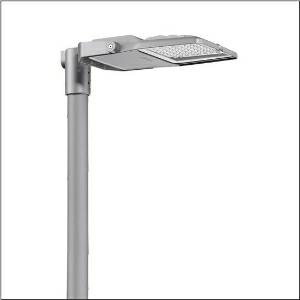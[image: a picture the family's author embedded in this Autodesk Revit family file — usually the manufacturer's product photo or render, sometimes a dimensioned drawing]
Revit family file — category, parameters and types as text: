
# Revit family: floodlight_fl_21_mini___pl43_5xa7775c2a3a_cdc0
name_source: partatom
category: Lighting Fixtures
units: mm (PartAtom-declared; Revit-internal decimal feet)

## family parameters
Cut with Voids When Loaded = No
Host = Face
Light Source = No
Part Type = Normal
Room Calculation Point = No
Round Connector Dimension = Use Diameter
Shared = No

## types (1)
- --- (1 x LED, 12500 lm, 89 W, 3000K)
    Apparent Load = 89 VA
    CIE Flux Codes = 27 78 99 100 100
    Color Rendering = 70
    Color Temperature = 3000K
    Default Elevation = 1800 mm
    Description = Floodlight FL 21 mini, floodlight, primary light control with lens, of PMMA, primary optical cover: protective disc, of toughened safety glass, transparent, light distribution: PL43, light emission: direct distribution, installation type: surface-mounted, LED, High Power LED, rated luminous flux: 12.500lm, luminous efficacy: 140lm/W, light colour: 730, colour temperature: 3000K, control gear: ECG Smart Interface, control: flexible luminous flux parameterisation, time-dependent luminous flux control, constant luminous flux control, overheat protection, presetting dimming logarithmic, with terminal, 6-pole, mains connection: 220..240V, AC, 50/60Hz, start of lifetime: 89W, end of lifetime: 94W, reduction: 43W, luminaire housing, of diecast aluminium, powder-coated, Siteco® metallic grey (DB 702S), corrosivity category C5 according to DIN EN ISO 12944, mast bracket, of steel, galvanised, powder-coated, Siteco® metallic grey (DB 702S), protection rating (complete): IP66, insulation class (complete): insulation class II (safety insulation), certification: CE, ENEC, VDE, protection symbol: D, impact resistance: IK08, permissible operating ambient temperature: -40..+40°C, permissible operating ambient temperature for outdoor applications: -40..+50°C, standard: DIN EN 12944, packaging unit: 1 piece

Light Distribution: PL43
    Height = 70 mm
    Lamp = 1 x LED
    Lamp Light Flux = 12500 lm
    Lamp Power = 89 W
    Lamp count = 1
    Length = 485 mm
    Luminous efficacy = 140 lm/W
    Manufacturer = Siteco
    ModVariant = No
    Model = 5XA7775C2A3A
    Number of Poles = 1
    OnlyDefault = Yes
    Power Factor = 1
    Product Name = Floodlight FL 21 mini | PL43
    Product group = floodlight | pylon top
    ProductGroupID = 6101
    Protection Class = Protection class II
    Protection Degree = IP 66
    RLX_Detail_Level = 1
    RlxData = <blob elided: 100649 chars, md5=5cee6004>
    Socket = socket
    Standby Power = 0 W
    System Light Flux = 12500 lm
    System Power = 89 W
    Type Comments = factory setting: luminous flux: 100 % | dim-lin: 254 | 456 mA
    Type Image = l_1007125.jpg
    URL = http://relux.com
    VarID = @adj_072383
    Voltage = 0 V
    Weight = 0.00 kg
    Width = 337 mm

## geometry (parser evidence)
native form markers: Blend x4, Sweep x10
no freeform markers — native parametric forms only
